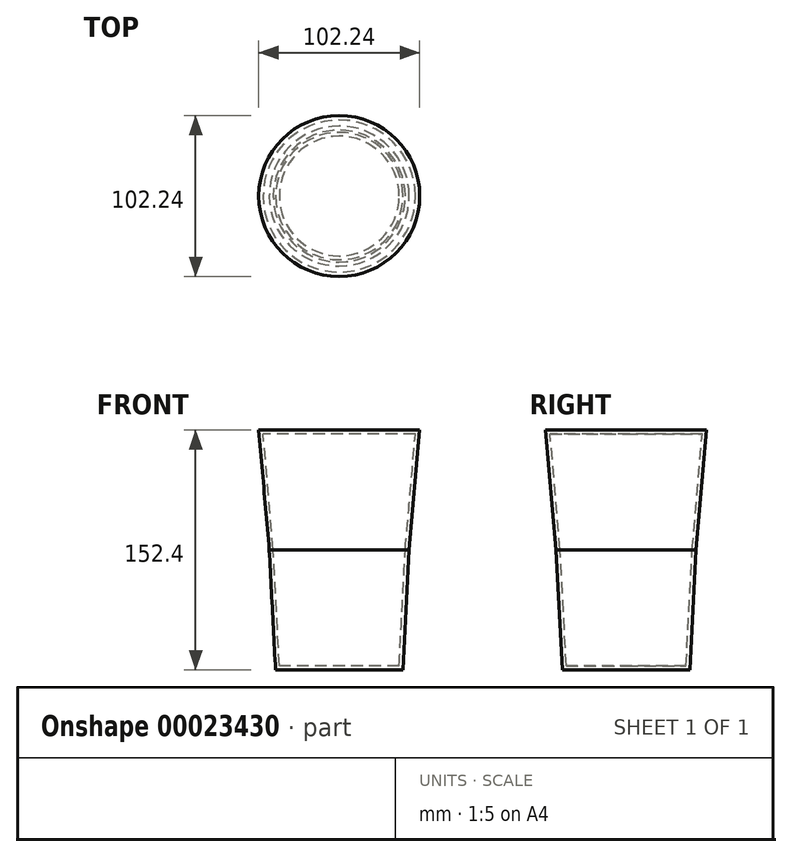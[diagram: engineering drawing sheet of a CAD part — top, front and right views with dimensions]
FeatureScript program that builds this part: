
annotation { "Feature Type Name" : "Feature", "Feature Type Description" : "" }
export const myFeature = defineFeature(function(context is Context, id is Id, definition is map)
    precondition{}
    {
        {
            var Q0;
            Q0=qCreatedBy(makeId("Top.planeOp"),FACE);
            var sketch = newSketch(context, id + "F0", { "sketchPlane" : qUnion([Q0])});
            skCircle(sketch, "E0", {"center": v(0, 0) * mm, "radius": 44.45 * mm});
            skSolve(sketch);
        }
        {
            var Q0;
            Q0 = qSketchRegion(id + "F0", true);
            extrude(context, id + "F1", {"entities" : qUnion([Q0]), "oppositeDirection" : true, "depth" : 76.2 * mm, "hasDraft" : true, "draftAngle" : 3 * degree, "draftPullDirection" : true, "hasSecondDirection" : true, "secondDirectionOppositeDirection" : false, "secondDirectionDepth" : 76.2 * mm, "hasSecondDirectionDraft" : true, "secondDirectionDraftAngle" : 5 * degree});
        }
        {
            var Q0;
            Q0=makeQuery(id+"F1.split0.splitOp","SPLIT",FACE,{"derivedFrom":makeQuery(id+"F1.opExtrude","SWEPT_FACE",FACE,{"disambiguationData":[OSD([sQuery(id+"F0.wireOp",EDGE,"E0")])]}),"isFromBackBody":true});
            var Q1;
            Q1=makeQuery(id+"F1.split0.splitOp","SPLIT",BODY,{"derivedFrom":makeQuery(id+"F1.opExtrude","SWEPT_BODY",BODY,{"disambiguationData":[OSD([sQuery(id+"F0.wireOp",EDGE,"E0")])]})});
            shell(context, id + "F2", {"isHollow" : true, "entities" : qUnion([Q0]), "parts" : qUnion([Q1]), "thickness" : 2.54 * mm});
        }
    });
